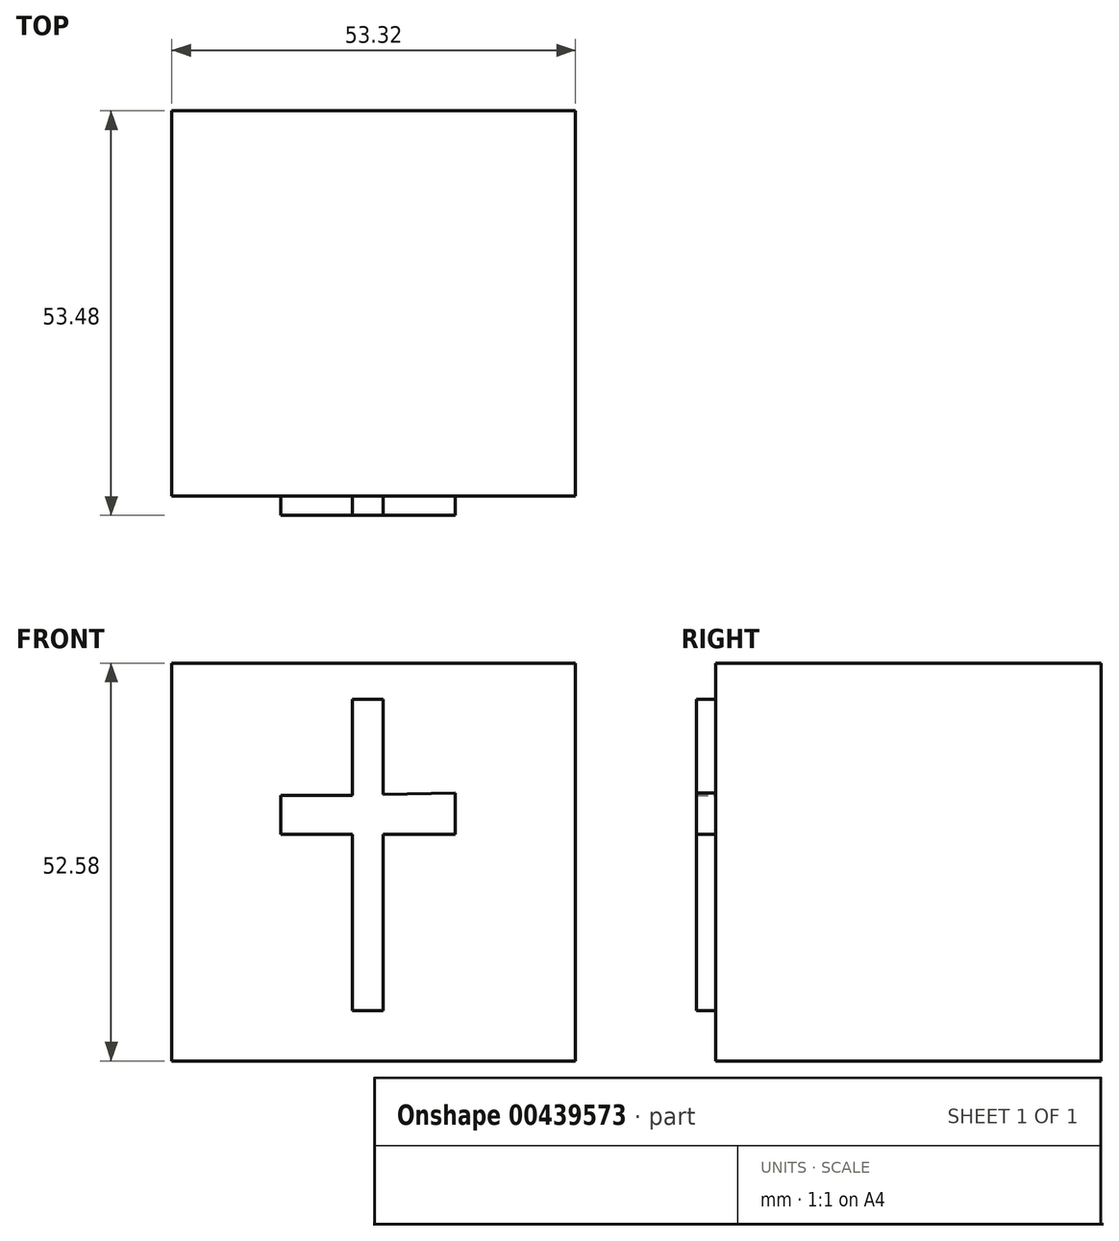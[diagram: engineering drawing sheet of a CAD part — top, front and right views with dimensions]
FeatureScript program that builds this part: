
annotation { "Feature Type Name" : "Feature", "Feature Type Description" : "" }
export const myFeature = defineFeature(function(context is Context, id is Id, definition is map)
    precondition{}
    {
        {
            var Q0;
            Q0=qCreatedBy(makeId("Top.planeOp"),FACE);
            var sketch = newSketch(context, id + "F0", { "sketchPlane" : qUnion([Q0])});
            skLineSegment(sketch, "E0.bottom", {"start": v(-75.98, 75.7) * mm, "end": v(-22.66, 75.7) * mm});
            skLineSegment(sketch, "E0.top", {"start": v(-75.98, 24.75) * mm, "end": v(-22.66, 24.75) * mm});
            skLineSegment(sketch, "E0.left", {"start": v(-75.98, 75.7) * mm, "end": v(-75.98, 24.75) * mm});
            skLineSegment(sketch, "E0.right", {"start": v(-22.66, 75.7) * mm, "end": v(-22.66, 24.75) * mm});
            skSolve(sketch);
        }
        {
            var Q0;
            Q0 = qSketchRegion(id + "F0", true);
            extrude(context, id + "F1", {"entities" : qUnion([Q0]), "depth" : 52.58 * mm});
        }
        {
            var Q0;
            Q0=makeQuery(id+"F1.opExtrude","SWEPT_FACE",FACE,{"disambiguationData":[OSD([sQuery(id+"F0.wireOp",EDGE,"E0.top")])]});
            var sketch = newSketch(context, id + "F2", { "sketchPlane" : qUnion([Q0])});
            skLineSegment(sketch, "E1", {"start": v(-52.1, 47.78) * mm, "end": v(-52.1, 6.62) * mm});
            skLineSegment(sketch, "E2", {"start": v(-52.1, 6.62) * mm, "end": v(-48.06, 6.62) * mm});
            skLineSegment(sketch, "E3", {"start": v(-48.06, 6.62) * mm, "end": v(-48.06, 47.78) * mm});
            skLineSegment(sketch, "E4", {"start": v(-48.06, 47.78) * mm, "end": v(-52.1, 47.78) * mm});
            skLineSegment(sketch, "E5", {"start": v(-52.1, 35.11) * mm, "end": v(-61.6, 35.11) * mm});
            skLineSegment(sketch, "E6", {"start": v(-61.6, 35.11) * mm, "end": v(-61.6, 29.93) * mm});
            skLineSegment(sketch, "E7", {"start": v(-61.6, 29.93) * mm, "end": v(-38.57, 29.93) * mm});
            skLineSegment(sketch, "E8", {"start": v(-38.57, 29.93) * mm, "end": v(-38.57, 35.4) * mm});
            skLineSegment(sketch, "E9", {"start": v(-38.57, 35.4) * mm, "end": v(-52.1, 35.11) * mm});
            skSolve(sketch);
        }
        {
            var Q0;
            {var subQ0=sQuery(id+"F2.wireOp",EDGE,"E5");Q0=makeQuery(id+"F2.imprint","IMPRINT",FACE,{"disambiguationData":[TD([[makeQuery(id+"F2.imprint","IMPRINT",EDGE,{"derivedFrom":subQ0}),1.0]])]});}
            var Q1;
            {var subQ3=sQuery(id+"F2.wireOp",EDGE,"E7");var subQ5=sQuery(id+"F2.wireOp",EDGE,"E3");var subQ6=makeQuery(id+"F2.imprint","INTERSECT",VERTEX,{"derivedFrom":[subQ5,subQ3]});Q1=makeQuery(id+"F2.imprint","IMPRINT",FACE,{"disambiguationData":[TD([[makeQuery(id+"F2.imprint","IMPRINT",EDGE,{"disambiguationData":[TD([[subQ6,-1.0]])],"derivedFrom":subQ5}),1.0]])]});}
            var Q2;
            {var subQ5=sQuery(id+"F2.wireOp",EDGE,"E8");Q2=makeQuery(id+"F2.imprint","IMPRINT",FACE,{"disambiguationData":[TD([[makeQuery(id+"F2.imprint","IMPRINT",EDGE,{"derivedFrom":subQ5}),1.0]])]});}
            var Q3;
            {var subQ0=sQuery(id+"F2.wireOp",EDGE,"E2");Q3=makeQuery(id+"F2.imprint","IMPRINT",FACE,{"disambiguationData":[TD([[makeQuery(id+"F2.imprint","IMPRINT",EDGE,{"derivedFrom":subQ0}),1.0]])]});}
            var Q4;
            {var subQ0=sQuery(id+"F2.wireOp",EDGE,"E4");Q4=makeQuery(id+"F2.imprint","IMPRINT",FACE,{"disambiguationData":[TD([[makeQuery(id+"F2.imprint","IMPRINT",EDGE,{"derivedFrom":subQ0}),1.0]])]});}
            extrude(context, id + "F3", {"entities" : qUnion([Q0, Q1, Q2, Q3, Q4]), "operationType" : NewBodyOperationType.ADD, "depth" : 2.54 * mm});
        }
    });
